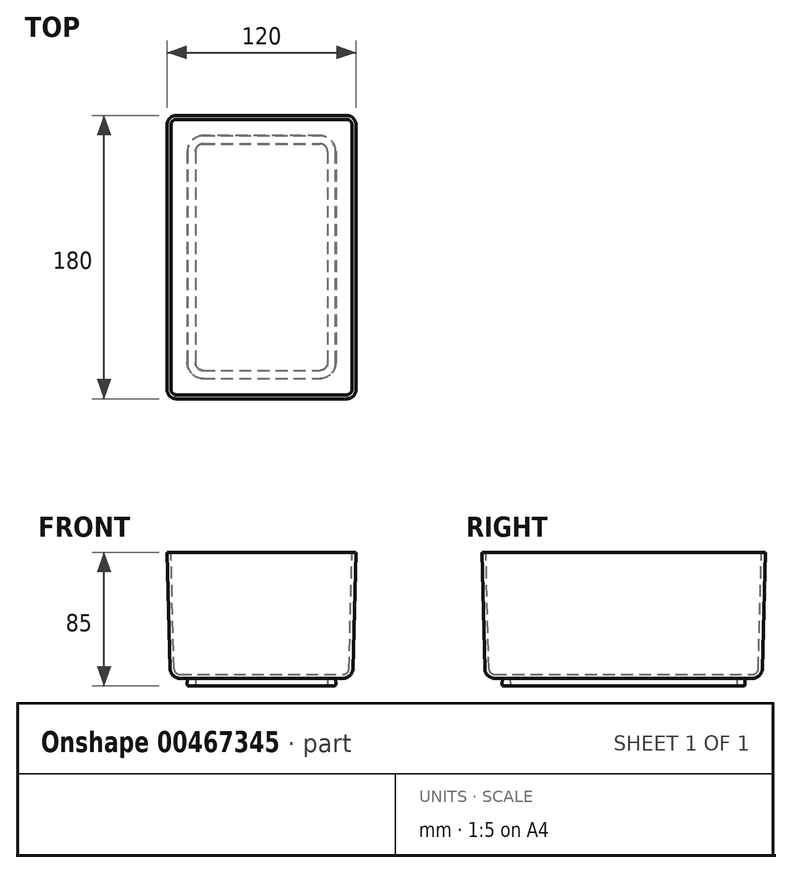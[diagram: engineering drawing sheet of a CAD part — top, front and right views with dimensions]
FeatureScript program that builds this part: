
annotation { "Feature Type Name" : "Feature", "Feature Type Description" : "" }
export const myFeature = defineFeature(function(context is Context, id is Id, definition is map)
    precondition{}
    {
        {
            var Q0;
            Q0=qCreatedBy(makeId("Top.planeOp"),FACE);
            var sketch = newSketch(context, id + "F0", { "sketchPlane" : qUnion([Q0])});
            skLineSegment(sketch, "E0.bottom", {"start": v(60, 90) * mm, "end": v(-60, 90) * mm});
            skLineSegment(sketch, "E0.top", {"start": v(60, -90) * mm, "end": v(-60, -90) * mm});
            skLineSegment(sketch, "E0.left", {"start": v(60, 90) * mm, "end": v(60, -90) * mm});
            skLineSegment(sketch, "E0.right", {"start": v(-60, 90) * mm, "end": v(-60, -90) * mm});
            skPoint(sketch, "E0.middle", {"position": v(0, 0) * mm});
            skSolve(sketch);
        }
        {
            var Q0;
            Q0 = qSketchRegion(id + "F0", true);
            extrude(context, id + "F1", {"entities" : qUnion([Q0]), "oppositeDirection" : true, "depth" : 80 * mm, "hasDraft" : true, "draftAngle" : 1.5 * degree, "draftPullDirection" : true});
        }
        {
            var Q0;
            Q0=makeQuery(id+"F1.opExtrude","SWEPT_EDGE",EDGE,{"disambiguationData":[OSD([sQuery(id+"F0.wireOp",EDGE,"E0.top"),sQuery(id+"F0.wireOp",EDGE,"E0.left")])]});
            var Q1;
            Q1=makeQuery(id+"F1.opExtrude","SWEPT_EDGE",EDGE,{"disambiguationData":[OSD([sQuery(id+"F0.wireOp",EDGE,"E0.top"),sQuery(id+"F0.wireOp",EDGE,"E0.right")])]});
            var Q2;
            Q2=makeQuery(id+"F1.opExtrude","SWEPT_EDGE",EDGE,{"disambiguationData":[OSD([sQuery(id+"F0.wireOp",EDGE,"E0.bottom"),sQuery(id+"F0.wireOp",EDGE,"E0.left")])]});
            var Q3;
            Q3=makeQuery(id+"F1.opExtrude","SWEPT_EDGE",EDGE,{"disambiguationData":[OSD([sQuery(id+"F0.wireOp",EDGE,"E0.bottom"),sQuery(id+"F0.wireOp",EDGE,"E0.right")])]});
            var Q4;
            Q4=makeQuery(id+"F1.opExtrude","CAP_FACE",FACE,{"disambiguationData":[OSD([sQuery(id+"F0.wireOp",EDGE,"E0.bottom"),sQuery(id+"F0.wireOp",EDGE,"E0.top"),sQuery(id+"F0.wireOp",EDGE,"E0.left"),sQuery(id+"F0.wireOp",EDGE,"E0.right")])],"isStart":false});
            fillet(context, id + "F2", {"entities" : qUnion([Q0, Q1, Q2, Q3, Q4]), "radius" : 6 * mm, "tangentPropagation" : true, "allowEdgeOverflow" : false});
        }
        {
            var Q0;
            Q0=makeQuery(id+"F1.opExtrude","CAP_FACE",FACE,{"disambiguationData":[OSD([sQuery(id+"F0.wireOp",EDGE,"E0.bottom"),sQuery(id+"F0.wireOp",EDGE,"E0.top"),sQuery(id+"F0.wireOp",EDGE,"E0.left"),sQuery(id+"F0.wireOp",EDGE,"E0.right")])],"isStart":true});
            shell(context, id + "F3", {"entities" : qUnion([Q0]), "thickness" : 2.5 * mm});
        }
        {
            var Q0;
            Q0=makeQuery(id+"F1.opExtrude","CAP_FACE",FACE,{"disambiguationData":[OSD([sQuery(id+"F0.wireOp",EDGE,"E0.bottom"),sQuery(id+"F0.wireOp",EDGE,"E0.top"),sQuery(id+"F0.wireOp",EDGE,"E0.left"),sQuery(id+"F0.wireOp",EDGE,"E0.right")])],"isStart":false});
            var sketch = newSketch(context, id + "F4", { "sketchPlane" : qUnion([Q0])});
            skLineSegment(sketch, "E1.bottom", {"start": v(-52.06, -82.06) * mm, "end": v(52.06, -82.06) * mm, "construction": true});
            skLineSegment(sketch, "E1.top", {"start": v(-52.06, 82.06) * mm, "end": v(52.06, 82.06) * mm, "construction": true});
            skLineSegment(sketch, "E1.left", {"start": v(-52.06, -82.06) * mm, "end": v(-52.06, 82.06) * mm, "construction": true});
            skLineSegment(sketch, "E1.right", {"start": v(52.06, -82.06) * mm, "end": v(52.06, 82.06) * mm, "construction": true});
            skLineSegment(sketch, "E2.0", {"start": v(-47.06, -67.06) * mm, "end": v(-47.06, 67.06) * mm});
            skLineSegment(sketch, "E2.1", {"start": v(-37.06, -77.06) * mm, "end": v(37.06, -77.06) * mm});
            skLineSegment(sketch, "E2.2", {"start": v(47.06, -67.06) * mm, "end": v(47.06, 67.06) * mm});
            skLineSegment(sketch, "E2.3", {"start": v(-37.06, 77.06) * mm, "end": v(37.06, 77.06) * mm});
            skPoint(sketch, "E3.visualSharp", {"position": v(-47.06, -77.06) * mm});
            skArc(sketch, "E3.filletArc", {"start": v(-47.06, -67.06) * mm, "mid": v(-44.13, -74.13) * mm, "end": v(-37.06, -77.06) * mm});
            skPoint(sketch, "E4.visualSharp", {"position": v(-47.06, 77.06) * mm});
            skArc(sketch, "E4.filletArc", {"start": v(-37.06, 77.06) * mm, "mid": v(-44.13, 74.13) * mm, "end": v(-47.06, 67.06) * mm});
            skPoint(sketch, "E5.visualSharp", {"position": v(47.06, -77.06) * mm});
            skArc(sketch, "E5.filletArc", {"start": v(37.06, -77.06) * mm, "mid": v(44.13, -74.13) * mm, "end": v(47.06, -67.06) * mm});
            skPoint(sketch, "E6.visualSharp", {"position": v(47.06, 77.06) * mm});
            skArc(sketch, "E6.filletArc", {"start": v(47.06, 67.06) * mm, "mid": v(44.13, 74.13) * mm, "end": v(37.06, 77.06) * mm});
            skArc(sketch, "E7.0", {"start": v(-42.06, -67.06) * mm, "mid": v(-40.6, -70.6) * mm, "end": v(-37.06, -72.06) * mm});
            skLineSegment(sketch, "E7.1", {"start": v(-42.06, -67.06) * mm, "end": v(-42.06, 67.06) * mm});
            skLineSegment(sketch, "E7.2", {"start": v(-37.06, -72.06) * mm, "end": v(37.06, -72.06) * mm});
            skArc(sketch, "E7.3", {"start": v(-37.06, 72.06) * mm, "mid": v(-40.6, 70.6) * mm, "end": v(-42.06, 67.06) * mm});
            skArc(sketch, "E7.4", {"start": v(37.06, -72.06) * mm, "mid": v(40.6, -70.6) * mm, "end": v(42.06, -67.06) * mm});
            skLineSegment(sketch, "E7.5", {"start": v(42.06, -67.06) * mm, "end": v(42.06, 67.06) * mm});
            skArc(sketch, "E7.6", {"start": v(42.06, 67.06) * mm, "mid": v(40.6, 70.6) * mm, "end": v(37.06, 72.06) * mm});
            skLineSegment(sketch, "E7.7", {"start": v(-37.06, 72.06) * mm, "end": v(37.06, 72.06) * mm});
            skSolve(sketch);
        }
        {
            var Q0;
            Q0=makeQuery(id+"F4.imprint","IMPRINT",FACE,{"disambiguationData":[TD([[makeQuery(id+"F4.imprint","IMPRINT",EDGE,{"derivedFrom":sQuery(id+"F4.wireOp",EDGE,"E2.0")}),-1.0]])]});
            var Q1;
            Q1 = qConstructionFilter(qBodyType(qCreatedBy(id + "F4" ,EDGE), BodyType.WIRE), ConstructionObject.NO);
            extrude(context, id + "F5", {"entities" : qUnion([Q0]), "operationType" : NewBodyOperationType.ADD, "surfaceEntities" : qUnion([Q1]), "depth" : 5 * mm, "hasDraft" : true, "draftAngle" : 1.5 * degree});
        }
        {
            var Q0;
            Q0=makeQuery(id+"F5.opExtrude","CAP_EDGE",EDGE,{"disambiguationData":[OSD([sQuery(id+"F4.wireOp",EDGE,"E2.0")])],"isStart":true});
            var Q1;
            Q1=makeQuery(id+"F5.opExtrude","CAP_EDGE",EDGE,{"disambiguationData":[OSD([sQuery(id+"F4.wireOp",EDGE,"E3.filletArc")])],"isStart":false});
            var Q2;
            Q2=makeQuery(id+"F5.opExtrude","CAP_EDGE",EDGE,{"disambiguationData":[OSD([sQuery(id+"F4.wireOp",EDGE,"E7.2")])],"isStart":false});
            var Q3;
            Q3=makeQuery(id+"F5.opExtrude","CAP_EDGE",EDGE,{"disambiguationData":[OSD([sQuery(id+"F4.wireOp",EDGE,"E7.5")])],"isStart":true});
            fillet(context, id + "F6", {"entities" : qUnion([Q0, Q1, Q2, Q3]), "radius" : 1 * mm, "tangentPropagation" : true, "allowEdgeOverflow" : false});
        }
    });
